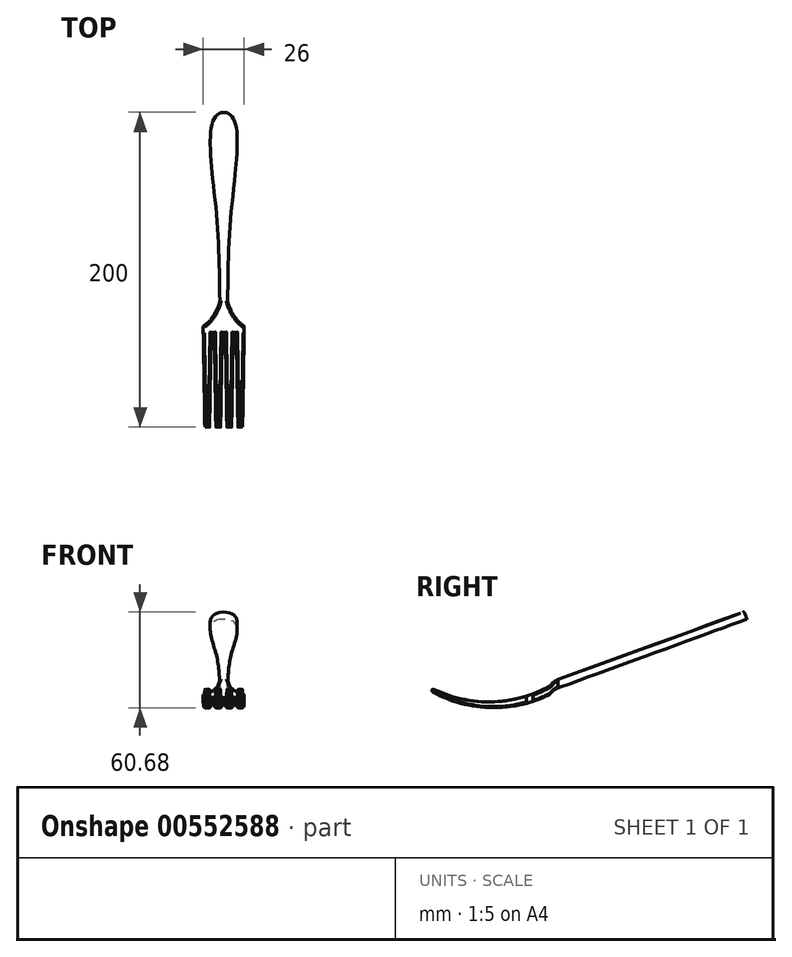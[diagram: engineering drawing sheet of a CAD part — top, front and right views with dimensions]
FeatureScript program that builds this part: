
annotation { "Feature Type Name" : "Feature", "Feature Type Description" : "" }
export const myFeature = defineFeature(function(context is Context, id is Id, definition is map)
    precondition{}
    {
        {
            var Q0;
            Q0=qCreatedBy(makeId("Right.planeOp"),FACE);
            var sketch = newSketch(context, id + "F0", { "sketchPlane" : qUnion([Q0])});
            skLineSegment(sketch, "E0", {"start": v(0, 0) * mm, "end": v(120, 43.68) * mm});
            skLineSegment(sketch, "E1", {"start": v(0, 0) * mm, "end": v(120, 0) * mm, "construction": true});
            skLineSegment(sketch, "E2", {"start": v(120, 0) * mm, "end": v(120, 43.68) * mm, "construction": true});
            skArc(sketch, "E3", {"start": v(0, 0) * mm, "mid": v(-2.83, -1.6) * mm, "end": v(-5, -4) * mm});
            skArc(sketch, "E4", {"start": v(-80, -2.34) * mm, "mid": v(-42.7, -12.5) * mm, "end": v(-5, -4) * mm});
            skLineSegment(sketch, "E5", {"start": v(120, 43.68) * mm, "end": v(118.29, 48.37) * mm});
            skPoint(sketch, "E6.endSnap0", {"position": v(-42.5, -13.34) * mm});
            skLineSegment(sketch, "E7", {"start": v(-42.5, -13.34) * mm, "end": v(-42.5, 1) * mm, "construction": true});
            skLineSegment(sketch, "E8", {"start": v(-80, -2.34) * mm, "end": v(-80, -0.34) * mm});
            skLineSegment(sketch, "E9", {"start": v(0, 5.32) * mm, "end": v(118.29, 48.37) * mm});
            skArc(sketch, "E10", {"start": v(0, 5.32) * mm, "mid": v(-2.83, 3.73) * mm, "end": v(-5, 1.32) * mm});
            skArc(sketch, "E11", {"start": v(-80, -0.34) * mm, "mid": v(-42.3, -8.85) * mm, "end": v(-5, 1.32) * mm});
            skLineSegment(sketch, "E12", {"start": v(0, 0) * mm, "end": v(0, 5.32) * mm});
            skLineSegment(sketch, "E13", {"start": v(-5, -4) * mm, "end": v(-88.36, -4) * mm, "construction": true});
            skLineSegment(sketch, "E14", {"start": v(-5, 1.32) * mm, "end": v(-88.36, 1.32) * mm, "construction": true});
            skLineSegment(sketch, "E15", {"start": v(-82.74, -4) * mm, "end": v(-82.74, 1.32) * mm, "construction": true});
            skLineSegment(sketch, "E16", {"start": v(-82.74, -4) * mm, "end": v(-82.74, -1.34) * mm, "construction": true});
            skLineSegment(sketch, "E17", {"start": v(-82.74, -1.34) * mm, "end": v(-67.29, -1.34) * mm, "construction": true});
            skSolve(sketch);
        }
        {
            var Q0;
            Q0=makeQuery(id+"F0.imprint","IMPRINT",FACE,{"disambiguationData":[TD([[makeQuery(id+"F0.imprint","IMPRINT",EDGE,{"derivedFrom":sQuery(id+"F0.wireOp",EDGE,"E0")}),1.0]])]});
            extrude(context, id + "F1", {"entities" : qUnion([Q0]), "depth" : 20 * mm, "offsetDistance" : 25 * mm, "symmetric" : true});
        }
        {
            var Q0;
            Q0=makeQuery(id+"F0.imprint","IMPRINT",FACE,{"disambiguationData":[TD([[makeQuery(id+"F0.imprint","IMPRINT",EDGE,{"derivedFrom":sQuery(id+"F0.wireOp",EDGE,"E3")}),-1.0]])]});
            extrude(context, id + "F2", {"entities" : qUnion([Q0]), "operationType" : NewBodyOperationType.ADD, "depth" : 26 * mm, "offsetDistance" : 25 * mm, "symmetric" : true});
        }
        {
            var Q0;
            Q0=qCreatedBy(makeId("Top.planeOp"),FACE);
            cPlane(context, id + "F3", {"entities" : qUnion([Q0]), "cplaneType" : CPlaneType.OFFSET, "offset" : 100 * mm, "width" : 150 * mm, "height" : 150 * mm});
        }
        {
            var Q0;
            Q0=makeQuery(id+"F1.opExtrude","SWEPT_FACE",FACE,{"disambiguationData":[OSD([sQuery(id+"F0.wireOp",EDGE,"E9")])]});
            var sketch = newSketch(context, id + "F4", { "sketchPlane" : qUnion([Q0])});
            skLineSegment(sketch, "E18", {"start": v(0, 127.7) * mm, "end": v(0, 1.82) * mm, "construction": true});
            skLineSegment(sketch, "E19", {"start": v(0, 1.82) * mm, "end": v(-10, 64.76) * mm, "construction": true});
            skLineSegment(sketch, "E20", {"start": v(-10, 64.76) * mm, "end": v(0, 127.7) * mm, "construction": true});
            skLineSegment(sketch, "E21", {"start": v(0, 127.7) * mm, "end": v(10, 64.76) * mm, "construction": true});
            skLineSegment(sketch, "E22", {"start": v(10, 64.76) * mm, "end": v(0, 1.82) * mm, "construction": true});
            skLineSegment(sketch, "E23", {"start": v(-10, 64.76) * mm, "end": v(-10, 127.7) * mm, "construction": true});
            skLineSegment(sketch, "E24", {"start": v(-10, 127.7) * mm, "end": v(10, 127.7) * mm, "construction": true});
            skLineSegment(sketch, "E25", {"start": v(10, 127.7) * mm, "end": v(10, 64.76) * mm, "construction": true});
            skLineSegment(sketch, "E26", {"start": v(10, 96.23) * mm, "end": v(0, 127.7) * mm, "construction": true});
            skLineSegment(sketch, "E27", {"start": v(0, 127.7) * mm, "end": v(-10, 96.23) * mm, "construction": true});
            skLineSegment(sketch, "E28", {"start": v(-10, 127.7) * mm, "end": v(-10, 96.23) * mm, "construction": true});
            skLineSegment(sketch, "E29", {"start": v(0, 127.7) * mm, "end": v(-10, 111.97) * mm, "construction": true});
            skLineSegment(sketch, "E30", {"start": v(-10, 111.97) * mm, "end": v(10, 111.97) * mm, "construction": true});
            skLineSegment(sketch, "E31", {"start": v(10, 111.97) * mm, "end": v(0, 127.7) * mm, "construction": true});
            skLineSegment(sketch, "E32", {"start": v(0, 127.7) * mm, "end": v(-10, 121.35) * mm, "construction": true});
            skLineSegment(sketch, "E33", {"start": v(-10, 121.35) * mm, "end": v(10, 121.35) * mm, "construction": true});
            skLineSegment(sketch, "E34", {"start": v(10, 121.35) * mm, "end": v(0, 127.7) * mm, "construction": true});
            skLineSegment(sketch, "E35", {"start": v(10, 64.76) * mm, "end": v(-10, 64.76) * mm, "construction": true});
            skLineSegment(sketch, "E36", {"start": v(0, 64.76) * mm, "end": v(-10, 64.76) * mm, "construction": true});
            skLineSegment(sketch, "E37", {"start": v(10, 64.76) * mm, "end": v(0, 64.76) * mm, "construction": true});
            skLineSegment(sketch, "E38", {"start": v(10, 121.35) * mm, "end": v(7, 121.35) * mm, "construction": true});
            skLineSegment(sketch, "E39", {"start": v(-10, 121.35) * mm, "end": v(-7, 121.35) * mm, "construction": true});
            skLineSegment(sketch, "E40", {"start": v(0, 127.7) * mm, "end": v(0, 124.7) * mm, "construction": true});
            skLineSegment(sketch, "E41", {"start": v(0, 1.82) * mm, "end": v(-2.5, 1.82) * mm, "construction": true});
            skLineSegment(sketch, "E42", {"start": v(0, 1.82) * mm, "end": v(2.5, 1.82) * mm, "construction": true});
            skFitSpline(sketch, "E43", {"points": [v(2.5, 1.82) * mm, v(5, 64.76) * mm, v(7, 121.35) * mm, v(0, 127.7) * mm, v(-7, 121.35) * mm, v(-5, 64.76) * mm, v(-2.5, 1.82) * mm], "startDerivative": vector(2.8, 280.56) * mm, "endDerivative": vector(2.8, -280.56) * mm});
            skLineSegment(sketch, "E44", {"start": v(-2.5, 1.82) * mm, "end": v(-18.98, 1.82) * mm});
            skLineSegment(sketch, "E45", {"start": v(2.5, 1.82) * mm, "end": v(18.98, 1.82) * mm});
            skLineSegment(sketch, "E46", {"start": v(-18.98, 1.82) * mm, "end": v(-18.98, 148.78) * mm});
            skLineSegment(sketch, "E47", {"start": v(18.98, 1.82) * mm, "end": v(18.98, 148.78) * mm});
            skLineSegment(sketch, "E48", {"start": v(18.98, 148.78) * mm, "end": v(-18.98, 148.78) * mm});
            skSolve(sketch);
        }
        {
            var Q0;
            {var subQ4=sQuery(id+"F0.wireOp",EDGE,"E9");var subQ8=makeQuery(id+"F1.opExtrude","CAP_EDGE",EDGE,{"disambiguationData":[OSD([subQ4])],"isStart":false});Q0=makeQuery(id+"F4.imprint","IMPRINT",FACE,{"disambiguationData":[TD([[makeQuery(id+"F4.imprint","IMPRINT",EDGE,{"derivedFrom":subQ8}),1.0]])]});}
            var Q1;
            {var subQ4=sQuery(id+"F0.wireOp",EDGE,"E9");var subQ8=makeQuery(id+"F1.opExtrude","CAP_EDGE",EDGE,{"disambiguationData":[OSD([subQ4])],"isStart":true});Q1=makeQuery(id+"F4.imprint","IMPRINT",FACE,{"disambiguationData":[TD([[makeQuery(id+"F4.imprint","IMPRINT",EDGE,{"derivedFrom":subQ8}),-1.0]])]});}
            extrude(context, id + "F5", {"entities" : qUnion([Q0, Q1]), "operationType" : NewBodyOperationType.REMOVE, "endBound" : BoundingType.THROUGH_ALL, "oppositeDirection" : true, "depth" : 25 * mm, "offsetDistance" : 25 * mm});
        }
        {
            var Q0;
            Q0=makeQuery(id+"F1.opExtrude","CAP_FACE",FACE,{"disambiguationData":[OSD([sQuery(id+"F0.wireOp",EDGE,"E0"),sQuery(id+"F0.wireOp",EDGE,"E5"),sQuery(id+"F0.wireOp",EDGE,"E9"),sQuery(id+"F0.wireOp",EDGE,"E12")])],"isStart":false});
            var Q1;
            {var subQ0=sQuery(id+"F4.wireOp",EDGE,"E45");var subQ1=sQuery(id+"F4.wireOp",EDGE,"E43");var subQ4=sQuery(id+"F0.wireOp",EDGE,"E9");var subQ6=makeQuery(id+"F4.imprint","INTERSECT",VERTEX,{"derivedFrom":[makeQuery(id+"F1.opExtrude","SWEPT_EDGE",EDGE,{"disambiguationData":[OSD([sQuery(id+"F0.wireOp",EDGE,"E5"),subQ4])]}),subQ1]});Q1=makeQuery(id+"F5.boolean.opBoolean","INTERSECT",VERTEX,{"derivedFrom":[makeQuery(id+"F1.opExtrude","SWEPT_FACE",FACE,{"disambiguationData":[OSD([sQuery(id+"F0.wireOp",EDGE,"E0")])]}),makeQuery(id+"F5.opExtrude","SWEPT_FACE",FACE,{"disambiguationData":[OSD([subQ1]),TDD([makeQuery(id+"F4.imprint","IMPRINT",EDGE,{"disambiguationData":[TD([[subQ6,1.0]])],"derivedFrom":subQ1})])]}),makeQuery(id+"F5.opExtrude","SWEPT_FACE",FACE,{"disambiguationData":[OSD([subQ1]),TDD([makeQuery(id+"F4.imprint","IMPRINT",EDGE,{"disambiguationData":[TD([[subQ6,-1.0]])],"derivedFrom":subQ1})])]}),makeQuery(id+"F5.opExtrude","SWEPT_FACE",FACE,{"disambiguationData":[OSD([subQ0])]})]});}
            extrude(context, id + "F6", {"entities" : qUnion([Q0]), "operationType" : NewBodyOperationType.REMOVE, "endBound" : BoundingType.UP_TO_VERTEX, "oppositeDirection" : true, "depth" : 7.5 * mm, "endBoundEntityVertex" : qUnion([Q1]), "offsetDistance" : 25 * mm});
        }
        {
            var Q0;
            Q0=makeQuery(id+"F1.opExtrude","CAP_FACE",FACE,{"disambiguationData":[OSD([sQuery(id+"F0.wireOp",EDGE,"E0"),sQuery(id+"F0.wireOp",EDGE,"E5"),sQuery(id+"F0.wireOp",EDGE,"E9"),sQuery(id+"F0.wireOp",EDGE,"E12")])],"isStart":true});
            var Q1;
            {var subQ0=sQuery(id+"F4.wireOp",EDGE,"E44");var subQ1=sQuery(id+"F4.wireOp",EDGE,"E43");var subQ4=sQuery(id+"F0.wireOp",EDGE,"E9");var subQ6=makeQuery(id+"F4.imprint","INTERSECT",VERTEX,{"derivedFrom":[makeQuery(id+"F1.opExtrude","SWEPT_EDGE",EDGE,{"disambiguationData":[OSD([sQuery(id+"F0.wireOp",EDGE,"E5"),subQ4])]}),subQ1]});Q1=makeQuery(id+"F5.boolean.opBoolean","INTERSECT",VERTEX,{"derivedFrom":[makeQuery(id+"F1.opExtrude","SWEPT_FACE",FACE,{"disambiguationData":[OSD([sQuery(id+"F0.wireOp",EDGE,"E0")])]}),makeQuery(id+"F5.opExtrude","SWEPT_FACE",FACE,{"disambiguationData":[OSD([subQ1]),TDD([makeQuery(id+"F4.imprint","IMPRINT",EDGE,{"disambiguationData":[TD([[subQ6,1.0]])],"derivedFrom":subQ1})])]}),makeQuery(id+"F5.opExtrude","SWEPT_FACE",FACE,{"disambiguationData":[OSD([subQ1]),TDD([makeQuery(id+"F4.imprint","IMPRINT",EDGE,{"disambiguationData":[TD([[subQ6,-1.0]])],"derivedFrom":subQ1})])]}),makeQuery(id+"F5.opExtrude","SWEPT_FACE",FACE,{"disambiguationData":[OSD([subQ0])]})]});}
            extrude(context, id + "F7", {"entities" : qUnion([Q0]), "operationType" : NewBodyOperationType.REMOVE, "endBound" : BoundingType.UP_TO_VERTEX, "oppositeDirection" : true, "depth" : 25 * mm, "endBoundEntityVertex" : qUnion([Q1]), "offsetDistance" : 25 * mm});
        }
        {
            var Q0;
            Q0=qCreatedBy(id+"F3.planeOp",FACE);
            var sketch = newSketch(context, id + "F8", { "sketchPlane" : qUnion([Q0])});
            skLineSegment(sketch, "E49", {"start": v(0, 0) * mm, "end": v(0, -80) * mm, "construction": true});
            skPoint(sketch, "E50.endSnap0", {"position": v(0, -40) * mm});
            skLineSegment(sketch, "E51", {"start": v(0, 0) * mm, "end": v(-2.5, 0) * mm, "construction": true});
            skLineSegment(sketch, "E52", {"start": v(0, 0) * mm, "end": v(2.5, 0) * mm, "construction": true});
            skLineSegment(sketch, "E53", {"start": v(-2.5, 0) * mm, "end": v(-2.5, -2) * mm, "construction": true});
            skLineSegment(sketch, "E54", {"start": v(2.5, 0) * mm, "end": v(2.5, -2) * mm, "construction": true});
            skLineSegment(sketch, "E55", {"start": v(-2.5, -2) * mm, "end": v(-3, -2) * mm, "construction": true});
            skLineSegment(sketch, "E56", {"start": v(2.5, -2) * mm, "end": v(3, -2) * mm, "construction": true});
            skFitSpline(sketch, "E57", {"points": [v(-2.5, 0) * mm, v(-3, -2) * mm, v(-7.3, -10.4) * mm, v(-13, -16) * mm], "startDerivative": vector(-1.53, -7.66) * mm, "endDerivative": vector(-15.57, -12.07) * mm});
            skFitSpline(sketch, "E58", {"points": [v(2.5, 0) * mm, v(3, -2) * mm, v(7.3, -10.4) * mm, v(13, -16) * mm], "startDerivative": vector(1.53, -7.66) * mm, "endDerivative": vector(15.57, -12.07) * mm});
            skLineSegment(sketch, "E59", {"start": v(-2.5, 0) * mm, "end": v(-28.33, 0) * mm});
            skLineSegment(sketch, "E60", {"start": v(-28.33, 0) * mm, "end": v(-28.33, 0) * mm});
            skLineSegment(sketch, "E61", {"start": v(-28.33, 0) * mm, "end": v(28.33, 0) * mm});
            skLineSegment(sketch, "E62", {"start": v(28.33, 0) * mm, "end": v(28.33, 0) * mm});
            skLineSegment(sketch, "E63", {"start": v(28.33, 0) * mm, "end": v(2.5, 0) * mm});
            skLineSegment(sketch, "E64", {"start": v(12, -80) * mm, "end": v(-12, -80) * mm, "construction": true});
            skLineSegment(sketch, "E65", {"start": v(-12, -80) * mm, "end": v(-9, -80) * mm});
            skLineSegment(sketch, "E66", {"start": v(-9, -80) * mm, "end": v(-5, -80) * mm});
            skLineSegment(sketch, "E67", {"start": v(-5, -80) * mm, "end": v(-2, -80) * mm});
            skLineSegment(sketch, "E68", {"start": v(-2, -80) * mm, "end": v(2, -80) * mm, "construction": true});
            skLineSegment(sketch, "E69", {"start": v(2, -80) * mm, "end": v(5, -80) * mm});
            skLineSegment(sketch, "E70", {"start": v(5, -80) * mm, "end": v(9, -80) * mm, "construction": true});
            skLineSegment(sketch, "E71", {"start": v(12, -80) * mm, "end": v(9, -80) * mm});
            skLineSegment(sketch, "E72", {"start": v(-13, -16) * mm, "end": v(-13, -20) * mm});
            skLineSegment(sketch, "E73", {"start": v(13, -16) * mm, "end": v(13, -20) * mm});
            skLineSegment(sketch, "E74", {"start": v(-13, -20) * mm, "end": v(13, -20) * mm, "construction": true});
            skLineSegment(sketch, "E75", {"start": v(-13, -20) * mm, "end": v(-12, -80) * mm});
            skLineSegment(sketch, "E76", {"start": v(13, -20) * mm, "end": v(12, -80) * mm});
            skLineSegment(sketch, "E77", {"start": v(-9, -80) * mm, "end": v(-8, -20) * mm});
            skLineSegment(sketch, "E78", {"start": v(9, -80) * mm, "end": v(8, -20) * mm});
            skLineSegment(sketch, "E79", {"start": v(-5, -80) * mm, "end": v(-6, -20) * mm});
            skLineSegment(sketch, "E80", {"start": v(-2, -80) * mm, "end": v(-1, -20) * mm});
            skLineSegment(sketch, "E81", {"start": v(2, -80) * mm, "end": v(1, -20) * mm});
            skLineSegment(sketch, "E82", {"start": v(5, -80) * mm, "end": v(6, -20) * mm});
            skLineSegment(sketch, "E83", {"start": v(-6, -20) * mm, "end": v(-8, -20) * mm});
            skLineSegment(sketch, "E84", {"start": v(-1, -20) * mm, "end": v(1, -20) * mm});
            skLineSegment(sketch, "E85", {"start": v(6, -20) * mm, "end": v(8, -20) * mm});
            skLineSegment(sketch, "E86", {"start": v(-28.33, 0) * mm, "end": v(-28.33, -92.44) * mm});
            skLineSegment(sketch, "E87", {"start": v(-28.33, -92.44) * mm, "end": v(44.13, -92.44) * mm});
            skLineSegment(sketch, "E88", {"start": v(44.13, -92.44) * mm, "end": v(28.33, 0) * mm});
            skLineSegment(sketch, "E89", {"start": v(-9, -80) * mm, "end": v(-12, -80) * mm});
            skSolve(sketch);
        }
        {
            var Q0;
            Q0=makeQuery(id+"F8.imprint","IMPRINT",FACE,{"disambiguationData":[TD([[makeQuery(id+"F8.imprint","IMPRINT",EDGE,{"derivedFrom":sQuery(id+"F8.wireOp",EDGE,"E57")}),-1.0]])]});
            var Q1;
            Q1=makeQuery(id+"F8.imprint","IMPRINT",FACE,{"disambiguationData":[TD([[makeQuery(id+"F8.imprint","IMPRINT",EDGE,{"derivedFrom":sQuery(id+"F8.wireOp",EDGE,"E66")}),1.0]])]});
            extrude(context, id + "F9", {"entities" : qUnion([Q0, Q1]), "operationType" : NewBodyOperationType.REMOVE, "endBound" : BoundingType.THROUGH_ALL, "oppositeDirection" : true, "depth" : 25 * mm, "offsetDistance" : 25 * mm});
        }
        {
            var Q0;
            Q0=makeQuery(id+"F9.boolean.opBoolean","INTERSECT",EDGE,{"derivedFrom":[makeQuery(id+"F2.opExtrude","SWEPT_FACE",FACE,{"disambiguationData":[OSD([sQuery(id+"F0.wireOp",EDGE,"E10")])]}),makeQuery(id+"F9.opExtrude","SWEPT_FACE",FACE,{"disambiguationData":[OSD([sQuery(id+"F8.wireOp",EDGE,"E58")])]})]});
            var Q1;
            Q1=makeQuery(id+"F9.boolean.opBoolean","INTERSECT",EDGE,{"derivedFrom":[makeQuery(id+"F2.opExtrude","SWEPT_FACE",FACE,{"disambiguationData":[OSD([sQuery(id+"F0.wireOp",EDGE,"E10")])]}),makeQuery(id+"F9.opExtrude","SWEPT_FACE",FACE,{"disambiguationData":[OSD([sQuery(id+"F8.wireOp",EDGE,"E57")])]})]});
            var Q2;
            Q2=makeQuery(id+"F9.boolean.opBoolean","INTERSECT",EDGE,{"derivedFrom":[makeQuery(id+"F2.opExtrude","SWEPT_FACE",FACE,{"disambiguationData":[OSD([sQuery(id+"F0.wireOp",EDGE,"E3")])]}),makeQuery(id+"F9.opExtrude","SWEPT_FACE",FACE,{"disambiguationData":[OSD([sQuery(id+"F8.wireOp",EDGE,"E58")])]})]});
            var Q3;
            Q3=makeQuery(id+"F9.boolean.opBoolean","INTERSECT",EDGE,{"derivedFrom":[makeQuery(id+"F2.opExtrude","SWEPT_FACE",FACE,{"disambiguationData":[OSD([sQuery(id+"F0.wireOp",EDGE,"E3")])]}),makeQuery(id+"F9.opExtrude","SWEPT_FACE",FACE,{"disambiguationData":[OSD([sQuery(id+"F8.wireOp",EDGE,"E57")])]})]});
            var Q4;
            Q4=makeQuery(id+"F9.boolean.opBoolean","INTERSECT",EDGE,{"derivedFrom":[makeQuery(id+"F2.opExtrude","SWEPT_FACE",FACE,{"disambiguationData":[OSD([sQuery(id+"F0.wireOp",EDGE,"E11")])]}),makeQuery(id+"F9.opExtrude","SWEPT_FACE",FACE,{"disambiguationData":[OSD([sQuery(id+"F8.wireOp",EDGE,"E58")])]})]});
            var Q5;
            Q5=makeQuery(id+"F9.boolean.opBoolean","INTERSECT",EDGE,{"derivedFrom":[makeQuery(id+"F2.opExtrude","SWEPT_FACE",FACE,{"disambiguationData":[OSD([sQuery(id+"F0.wireOp",EDGE,"E4")])]}),makeQuery(id+"F9.opExtrude","SWEPT_FACE",FACE,{"disambiguationData":[OSD([sQuery(id+"F8.wireOp",EDGE,"E58")])]})]});
            var Q6;
            Q6=makeQuery(id+"F9.boolean.opBoolean","INTERSECT",EDGE,{"derivedFrom":[makeQuery(id+"F2.opExtrude","SWEPT_FACE",FACE,{"disambiguationData":[OSD([sQuery(id+"F0.wireOp",EDGE,"E11")])]}),makeQuery(id+"F9.opExtrude","SWEPT_FACE",FACE,{"disambiguationData":[OSD([sQuery(id+"F8.wireOp",EDGE,"E57")])]})]});
            var Q7;
            Q7=makeQuery(id+"F9.boolean.opBoolean","INTERSECT",EDGE,{"derivedFrom":[makeQuery(id+"F2.opExtrude","SWEPT_FACE",FACE,{"disambiguationData":[OSD([sQuery(id+"F0.wireOp",EDGE,"E4")])]}),makeQuery(id+"F9.opExtrude","SWEPT_FACE",FACE,{"disambiguationData":[OSD([sQuery(id+"F8.wireOp",EDGE,"E57")])]})]});
            var Q8;
            Q8=makeQuery(id+"F2.opExtrude","SWEPT_FACE",FACE,{"disambiguationData":[OSD([sQuery(id+"F0.wireOp",EDGE,"E11")])]});
            var Q9;
            Q9=makeQuery(id+"F2.opExtrude","SWEPT_FACE",FACE,{"disambiguationData":[OSD([sQuery(id+"F0.wireOp",EDGE,"E4")])]});
            var Q10;
            Q10=makeQuery(id+"F9.boolean.opBoolean","SPLIT",FACE,{"disambiguationData":[TD([makeQuery(id+"F9.opExtrude","SWEPT_FACE",FACE,{"disambiguationData":[OSD([sQuery(id+"F8.wireOp",EDGE,"Fos4u5P3-crwQ-TyGK-0RF0-8x8Drn4J1qq6")])]})])],"derivedFrom":makeQuery(id+"F2.opExtrude","SWEPT_FACE",FACE,{"disambiguationData":[OSD([sQuery(id+"F0.wireOp",EDGE,"E8")])]})});
            var Q11;
            Q11=makeQuery(id+"F9.boolean.opBoolean","SPLIT",FACE,{"disambiguationData":[TD([makeQuery(id+"F9.opExtrude","SWEPT_FACE",FACE,{"disambiguationData":[OSD([sQuery(id+"F8.wireOp",EDGE,"BNH5Uzot-W4mH-hyue-PTzn-nkNlBR71809Y")])]})])],"derivedFrom":makeQuery(id+"F2.opExtrude","SWEPT_FACE",FACE,{"disambiguationData":[OSD([sQuery(id+"F0.wireOp",EDGE,"E8")])]})});
            var Q12;
            Q12=makeQuery(id+"F9.boolean.opBoolean","SPLIT",FACE,{"disambiguationData":[TD([makeQuery(id+"F9.opExtrude","SWEPT_FACE",FACE,{"disambiguationData":[OSD([sQuery(id+"F8.wireOp",EDGE,"XtOzjEYh-kIgA-wWlO-W4R9-nihI3y1tmfr9")])]})])],"derivedFrom":makeQuery(id+"F2.opExtrude","SWEPT_FACE",FACE,{"disambiguationData":[OSD([sQuery(id+"F0.wireOp",EDGE,"E8")])]})});
            var Q13;
            Q13=makeQuery(id+"F9.boolean.opBoolean","SPLIT",FACE,{"disambiguationData":[TD([makeQuery(id+"F9.opExtrude","SWEPT_FACE",FACE,{"disambiguationData":[OSD([sQuery(id+"F8.wireOp",EDGE,"8pAi8bKF-4bC1-budy-TaaA-tgbljGODcZ9o")])]})])],"derivedFrom":makeQuery(id+"F2.opExtrude","SWEPT_FACE",FACE,{"disambiguationData":[OSD([sQuery(id+"F0.wireOp",EDGE,"E8")])]})});
            var Q14;
            Q14=makeQuery(id+"F7.boolean.opBoolean","COPY",EDGE,{"derivedFrom":makeQuery(id+"F7.opExtrude","TWEAK_EDGE",EDGE,{"derivedFrom":[makeQuery(id+"F1.opExtrude","CAP_EDGE",EDGE,{"disambiguationData":[OSD([sQuery(id+"F0.wireOp",EDGE,"E0")])],"isStart":true}),dummyQuery(id+"F7.vertexPlane.planeOp",FACE)]})});
            var Q15;
            Q15=makeQuery(id+"F6.boolean.opBoolean","COPY",EDGE,{"derivedFrom":makeQuery(id+"F6.opExtrude","TWEAK_EDGE",EDGE,{"derivedFrom":[makeQuery(id+"F1.opExtrude","CAP_EDGE",EDGE,{"disambiguationData":[OSD([sQuery(id+"F0.wireOp",EDGE,"E0")])],"isStart":false}),dummyQuery(id+"F6.vertexPlane.planeOp",FACE)]})});
            fillet(context, id + "F10", {"entities" : qUnion([Q0, Q1, Q2, Q3, Q4, Q5, Q6, Q7, Q8, Q9, Q10, Q11, Q12, Q13, Q14, Q15]), "radius" : 0.72 * mm, "tangentPropagation" : true, "allowEdgeOverflow" : false});
        }
        {
            var Q0;
            {var subQ0=sQuery(id+"F4.wireOp",EDGE,"E45");var subQ1=sQuery(id+"F0.wireOp",EDGE,"E12");var subQ2=sQuery(id+"F0.wireOp",EDGE,"E10");var subQ3=sQuery(id+"F0.wireOp",EDGE,"E9");Q0=makeQuery(id+"F10.opFillet","TWEAK_EDGE",EDGE,{"derivedFrom":[makeQuery(id+"F6.boolean.opBoolean","MERGE",VERTEX,{"derivedFrom":[makeQuery(id+"F5.boolean.opBoolean","COPY",VERTEX,{"derivedFrom":makeQuery(id+"F5.opExtrude","CAP_VERTEX",VERTEX,{"disambiguationData":[OSD([subQ3,subQ2,subQ1,sQuery(id+"F4.wireOp",EDGE,"E43"),subQ0])],"isStart":true})}),makeQuery(id+"F6.opExtrude","CAP_VERTEX",VERTEX,{"disambiguationData":[OSD([subQ3,subQ2,subQ1,subQ0,dummyQuery(id+"F6.vertexPlane.planeOp",FACE)])],"isStart":false})]})]});}
            var Q1;
            {var subQ0=sQuery(id+"F4.wireOp",EDGE,"E44");var subQ1=sQuery(id+"F0.wireOp",EDGE,"E12");var subQ2=sQuery(id+"F0.wireOp",EDGE,"E10");var subQ3=sQuery(id+"F0.wireOp",EDGE,"E9");Q1=makeQuery(id+"F10.opFillet","TWEAK_EDGE",EDGE,{"derivedFrom":[makeQuery(id+"F7.boolean.opBoolean","MERGE",VERTEX,{"derivedFrom":[makeQuery(id+"F5.boolean.opBoolean","COPY",VERTEX,{"derivedFrom":makeQuery(id+"F5.opExtrude","CAP_VERTEX",VERTEX,{"disambiguationData":[OSD([subQ3,subQ2,subQ1,sQuery(id+"F4.wireOp",EDGE,"E43"),subQ0])],"isStart":true})}),makeQuery(id+"F7.opExtrude","CAP_VERTEX",VERTEX,{"disambiguationData":[OSD([subQ3,subQ2,subQ1,subQ0,dummyQuery(id+"F7.vertexPlane.planeOp",FACE)])],"isStart":false})]})]});}
            fillet(context, id + "F11", {"entities" : qUnion([Q0, Q1]), "radius" : 0.78 * mm, "tangentPropagation" : true, "allowEdgeOverflow" : false});
        }
    });
